# Revit family: BC_Hitachi_Samurai-M-6075-LN_LOD400_
name_source: partatom
category: Mechanical Equipment
revit_build: Autodesk Revit 2018 (Build: 20170223_1515(x64)
units: mm (PartAtom-declared; Revit-internal decimal feet)

## family parameters
Always vertical = Yes
Classification = None
Cut with Voids When Loaded = No
Part Type = Normal
Room Calculation Point = No
Round Connector Dimension = Use Diameter
Shared = No
Work Plane-Based = No

## types (2) — shared parameters
BC_OBJECT_ID = 46958
BC_OBJECT_VERSION = #31
Description = Samurai M - Heat Pump Inverter Scroll (LN version) RHMA 18AN-N - RHMA 100AN-N
Frequency = 50 Hz
Inlet Water Diameter = 102 mm
Manufacturer = Hitachi Air Conditioning Europe SAS
MasterFormat = Central HVAC Equipment
Masterformat Code = 23 70 00
Model = Samurai M - Heat Pump Inverter Scroll (LN version)
Nominal Voltage = 400 V
Number of Poles = 3
OmniClass code = 23-33 21 13
OmniClass description = Chillers
Operating mode = Heating+Cooling
Overall height = 2500 mm
Overall length = 2240 mm
Overall width = 3050 mm
Refrigerant Type = R410A
Sound Power Low Noise (Cooling) = 82
Sound Power Low Noise (Heating) = 82
Sound Pressure at 10m (Cooling) = 53
Sound Pressure at 1m (Cooling) = 66
Uniformat = Cooling Generating Systems
Uniformat code = D3030
Water Outlet Diameter = 102 mm

## per-type parameters (varying)
| type | Airflow (High) | BC_VARIANT_ID | Coefficient of Performance (COP) | Cooling Capacity | Cooling Input Rated | Energy efficiency SCOP | Energy efficiency ratio (EER) | Heating Capacity | Heating Input Rated | Load of Refrigerant Fluid | Packing Weight | Rated Cooling Current | SEER energy efficiency | Starting current | Weight in operation |
| RHMA 60AN-N | 13664.4 L/s | 294250 | 3.1 | 157800 W | 52100 W | 3.54 | 2.03 | 155600 W | 50200 W | 29.50 kg | 1895.00 kg | 96 A | 4.06 | 248 A | 1922.00 kg |
| RHMA 75AN-N | 14950.3 L/s | 294251 | 3.08 | 181300 W | 61200 W | 3.53 | 2.96 | 180800 W | 58700 W | 32.00 kg | 1974.00 kg | 108 A | 4.39 | 261 A | 2003.00 kg |

note: column(s) folded — value = type name in every type: Product Code, Reference
